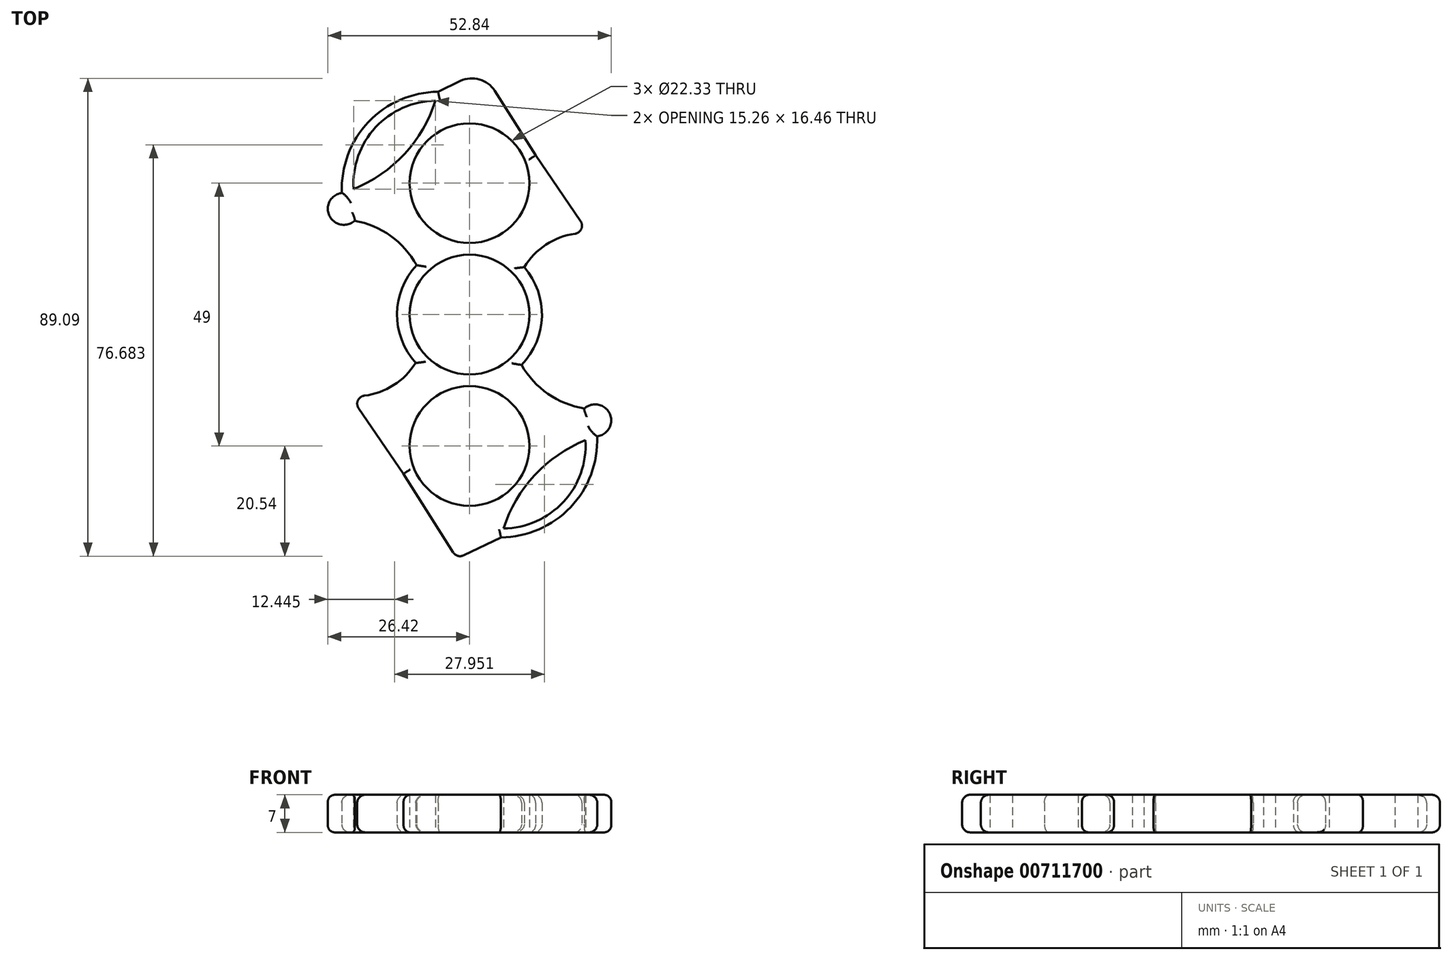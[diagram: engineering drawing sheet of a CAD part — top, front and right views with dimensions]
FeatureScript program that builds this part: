
annotation { "Feature Type Name" : "Feature", "Feature Type Description" : "" }
export const myFeature = defineFeature(function(context is Context, id is Id, definition is map)
    precondition{}
    {
        {
            var Q0;
            Q0=qCreatedBy(makeId("Top.planeOp"),FACE);
            var sketch = newSketch(context, id + "F0", { "sketchPlane" : qUnion([Q0])});
            skCircle(sketch, "E0", {"center": v(0, 0) * mm, "radius": 11.16 * mm});
            skCircle(sketch, "E1", {"center": v(0, 24.5) * mm, "radius": 11.16 * mm});
            skCircle(sketch, "E2", {"center": v(0, 24.5) * mm, "radius": 12.8 * mm});
            skCircle(sketch, "E3", {"center": v(0, 0) * mm, "radius": 13.5 * mm});
            skCircle(sketch, "E4.1.0", {"center": v(0, -24.5) * mm, "radius": 11.16 * mm});
            skCircle(sketch, "E4.1.1", {"center": v(0, -24.5) * mm, "radius": 12.8 * mm});
            skLineSegment(sketch, "E5", {"start": v(12.33, 29.7) * mm, "end": v(22.22, 15.2) * mm});
            skArc(sketch, "E6", {"start": v(-9.87, 9.2) * mm, "mid": v(-14.7, 14.68) * mm, "end": v(-21.43, 17.5) * mm});
            skArc(sketch, "E7", {"start": v(22.22, 15.2) * mm, "mid": v(15.33, 13.68) * mm, "end": v(10.2, 8.84) * mm});
            skArc(sketch, "E8.1.1", {"start": v(9.36, -8.73) * mm, "mid": v(14.33, -14.57) * mm, "end": v(21.43, -17.5) * mm});
            skLineSegment(sketch, "E8.1.2", {"start": v(-12.33, -29.7) * mm, "end": v(-22.22, -15.2) * mm});
            skArc(sketch, "E8.1.3", {"start": v(-22.22, -15.2) * mm, "mid": v(-14.95, -13.62) * mm, "end": v(-9.68, -8.38) * mm});
            skArc(sketch, "E9", {"start": v(-23.8, 22.69) * mm, "mid": v(-23.38, 16.73) * mm, "end": v(-23.15, 22.7) * mm});
            skArc(sketch, "E10", {"start": v(-23.13, 22.85) * mm, "mid": v(-12.1, 29.99) * mm, "end": v(-5.87, 41.55) * mm});
            skLineSegment(sketch, "E11", {"start": v(-5.87, 41.55) * mm, "end": v(2.3, 45.47) * mm});
            skPoint(sketch, "E12.orphan", {"position": v(0, 47.8) * mm});
            skArc(sketch, "E13.1.0", {"start": v(23.8, -22.69) * mm, "mid": v(23.38, -16.73) * mm, "end": v(23.15, -22.7) * mm});
            skArc(sketch, "E13.1.1", {"start": v(23.13, -22.85) * mm, "mid": v(12.1, -29.99) * mm, "end": v(5.87, -41.55) * mm});
            skLineSegment(sketch, "E13.1.2", {"start": v(5.87, -41.55) * mm, "end": v(-2.3, -45.47) * mm});
            skPoint(sketch, "E14.orphan", {"position": v(0, -47.8) * mm});
            skArc(sketch, "E15", {"start": v(-5.87, 41.55) * mm, "mid": v(-18.83, 35.92) * mm, "end": v(-23.8, 22.69) * mm});
            skArc(sketch, "E16.1.1", {"start": v(5.87, -41.55) * mm, "mid": v(18.83, -35.92) * mm, "end": v(23.8, -22.69) * mm});
            skPoint(sketch, "E17.orphan", {"position": v(-23.56, 22.71) * mm});
            skPoint(sketch, "E18.orphan", {"position": v(23.56, -22.71) * mm});
            skPoint(sketch, "E19.orphan", {"position": v(5.87, -41.55) * mm});
            skArc(sketch, "E20.trimOffspring", {"start": v(-23.13, 22.85) * mm, "mid": v(-23.14, 22.78) * mm, "end": v(-23.15, 22.7) * mm});
            skArc(sketch, "E21.trimOffspring", {"start": v(23.13, -22.85) * mm, "mid": v(23.14, -22.78) * mm, "end": v(23.15, -22.7) * mm});
            skArc(sketch, "E22", {"start": v(6.35, -39.87) * mm, "mid": v(17.5, -34.92) * mm, "end": v(21.6, -23.41) * mm});
            skArc(sketch, "E23.1.0", {"start": v(-6.35, 39.87) * mm, "mid": v(-17.5, 34.92) * mm, "end": v(-21.6, 23.41) * mm});
            skLineSegment(sketch, "E24", {"start": v(-23.15, 22.7) * mm, "end": v(-23.8, 22.69) * mm});
            skLineSegment(sketch, "E25", {"start": v(23.8, -22.69) * mm, "end": v(23.15, -22.7) * mm});
            skLineSegment(sketch, "E26", {"start": v(12.33, 29.7) * mm, "end": v(2.3, 45.47) * mm});
            skPoint(sketch, "E27.orphan", {"position": v(6.73, 47.59) * mm});
            skLineSegment(sketch, "E28.1.1", {"start": v(-12.33, -29.7) * mm, "end": v(-2.3, -45.47) * mm});
            skPoint(sketch, "E29.orphan", {"position": v(-6.73, -47.59) * mm});
            skSolve(sketch);
        }
        {
            var Q0;
            {var subQ0=sQuery(id+"F0.wireOp",EDGE,"E9");var subQ1=makeQuery(id+"F0.imprint","INTERSECT",VERTEX,{"derivedFrom":[sQuery(id+"F0.wireOp",EDGE,"E6"),subQ0]});Q0=makeQuery(id+"F0.imprint","IMPRINT",FACE,{"disambiguationData":[TD([[makeQuery(id+"F0.imprint","IMPRINT",EDGE,{"disambiguationData":[TD([[subQ1,1.0]])],"derivedFrom":subQ0}),1.0]])]});}
            var Q1;
            {var subQ0=sQuery(id+"F0.wireOp",EDGE,"E10");var subQ1=sQuery(id+"F0.wireOp",EDGE,"E9");var subQ2=makeQuery(id+"F0.imprint","INTERSECT",VERTEX,{"derivedFrom":[subQ1,subQ0]});Q1=makeQuery(id+"F0.imprint","IMPRINT",FACE,{"disambiguationData":[TD([[makeQuery(id+"F0.imprint","IMPRINT",EDGE,{"disambiguationData":[TD([[subQ2,-1.0]])],"derivedFrom":subQ1}),-1.0]])]});}
            var Q2;
            {var subQ0=sQuery(id+"F0.wireOp",EDGE,"E9");var subQ1=makeQuery(id+"F0.imprint","INTERSECT",VERTEX,{"derivedFrom":[subQ0,sQuery(id+"F0.wireOp",EDGE,"E10")]});Q2=makeQuery(id+"F0.imprint","IMPRINT",FACE,{"disambiguationData":[TD([[makeQuery(id+"F0.imprint","IMPRINT",EDGE,{"disambiguationData":[TD([[subQ1,1.0]])],"derivedFrom":subQ0}),1.0]])]});}
            var Q3;
            {var subQ0=sQuery(id+"F0.wireOp",EDGE,"E10");var subQ1=sQuery(id+"F0.wireOp",EDGE,"E9");var subQ2=makeQuery(id+"F0.imprint","INTERSECT",VERTEX,{"derivedFrom":[subQ1,subQ0]});Q3=makeQuery(id+"F0.imprint","IMPRINT",FACE,{"disambiguationData":[TD([[makeQuery(id+"F0.imprint","IMPRINT",EDGE,{"disambiguationData":[TD([[subQ2,1.0]])],"derivedFrom":subQ1}),-1.0]])]});}
            var Q4;
            {var subQ0=sQuery(id+"F0.wireOp",EDGE,"E13.1.1");var subQ1=sQuery(id+"F0.wireOp",EDGE,"E13.1.0");var subQ2=makeQuery(id+"F0.imprint","INTERSECT",VERTEX,{"derivedFrom":[subQ1,subQ0]});Q4=makeQuery(id+"F0.imprint","IMPRINT",FACE,{"disambiguationData":[TD([[makeQuery(id+"F0.imprint","IMPRINT",EDGE,{"disambiguationData":[TD([[subQ2,1.0]])],"derivedFrom":subQ1}),-1.0]])]});}
            var Q5;
            {var subQ0=sQuery(id+"F0.wireOp",EDGE,"E13.1.0");var subQ1=makeQuery(id+"F0.imprint","INTERSECT",VERTEX,{"derivedFrom":[subQ0,sQuery(id+"F0.wireOp",EDGE,"E13.1.1")]});Q5=makeQuery(id+"F0.imprint","IMPRINT",FACE,{"disambiguationData":[TD([[makeQuery(id+"F0.imprint","IMPRINT",EDGE,{"disambiguationData":[TD([[subQ1,1.0]])],"derivedFrom":subQ0}),1.0]])]});}
            var Q6;
            {var subQ0=sQuery(id+"F0.wireOp",EDGE,"E13.1.1");var subQ1=sQuery(id+"F0.wireOp",EDGE,"E13.1.0");var subQ2=makeQuery(id+"F0.imprint","INTERSECT",VERTEX,{"derivedFrom":[subQ1,subQ0]});Q6=makeQuery(id+"F0.imprint","IMPRINT",FACE,{"disambiguationData":[TD([[makeQuery(id+"F0.imprint","IMPRINT",EDGE,{"disambiguationData":[TD([[subQ2,-1.0]])],"derivedFrom":subQ1}),-1.0]])]});}
            var Q7;
            {var subQ10=sQuery(id+"F0.wireOp",EDGE,"E8.1.1");Q7=makeQuery(id+"F0.imprint","IMPRINT",FACE,{"disambiguationData":[TD([[makeQuery(id+"F0.imprint","IMPRINT",EDGE,{"derivedFrom":subQ10}),-1.0]])]});}
            var Q8;
            Q8=makeQuery(id+"F0.imprint","IMPRINT",FACE,{"disambiguationData":[TD([[makeQuery(id+"F0.imprint","IMPRINT",EDGE,{"derivedFrom":sQuery(id+"F0.wireOp",EDGE,"E4.1.0")}),-1.0]])]});
            var Q9;
            {var subQ0=sQuery(id+"F0.wireOp",EDGE,"E4.1.1");var subQ1=sQuery(id+"F0.wireOp",EDGE,"E3");var subQ2=makeQuery(id+"F0.imprint","INTERSECT",VERTEX,{"disambiguationData":[OD(0.0)],"derivedFrom":[subQ1,subQ0]});Q9=makeQuery(id+"F0.imprint","IMPRINT",FACE,{"disambiguationData":[TD([[makeQuery(id+"F0.imprint","IMPRINT",EDGE,{"disambiguationData":[TD([[subQ2,-1.0]])],"derivedFrom":subQ1}),1.0]])]});}
            var Q10;
            {var subQ0=sQuery(id+"F0.wireOp",EDGE,"E3");var subQ1=sQuery(id+"F0.wireOp",EDGE,"E2");var subQ2=makeQuery(id+"F0.imprint","INTERSECT",VERTEX,{"disambiguationData":[OD(0.0)],"derivedFrom":[subQ1,subQ0]});Q10=makeQuery(id+"F0.imprint","IMPRINT",FACE,{"disambiguationData":[TD([[makeQuery(id+"F0.imprint","IMPRINT",EDGE,{"disambiguationData":[TD([[subQ2,1.0]])],"derivedFrom":subQ1}),1.0]])]});}
            var Q11;
            Q11=makeQuery(id+"F0.imprint","IMPRINT",FACE,{"disambiguationData":[TD([[makeQuery(id+"F0.imprint","IMPRINT",EDGE,{"derivedFrom":sQuery(id+"F0.wireOp",EDGE,"E0")}),-1.0]])]});
            var Q12;
            Q12=makeQuery(id+"F0.imprint","IMPRINT",FACE,{"disambiguationData":[TD([[makeQuery(id+"F0.imprint","IMPRINT",EDGE,{"derivedFrom":sQuery(id+"F0.wireOp",EDGE,"E1")}),-1.0]])]});
            var Q13;
            Q13=makeQuery(id+"F0.imprint","IMPRINT",FACE,{"disambiguationData":[TD([[makeQuery(id+"F0.imprint","IMPRINT",EDGE,{"derivedFrom":sQuery(id+"F0.wireOp",EDGE,"E5")}),-1.0]])]});
            var Q14;
            {var subQ0=sQuery(id+"F0.wireOp",EDGE,"E13.1.0");var subQ1=makeQuery(id+"F0.imprint","INTERSECT",VERTEX,{"derivedFrom":[sQuery(id+"F0.wireOp",EDGE,"E8.1.1"),subQ0]});Q14=makeQuery(id+"F0.imprint","IMPRINT",FACE,{"disambiguationData":[TD([[makeQuery(id+"F0.imprint","IMPRINT",EDGE,{"disambiguationData":[TD([[subQ1,1.0]])],"derivedFrom":subQ0}),1.0]])]});}
            var Q15;
            {var subQ3=sQuery(id+"F0.wireOp",EDGE,"vcktaI46-IUl0-3yXv-VcWj-Kn2E1PGQpO04");Q15=makeQuery(id+"F0.imprint","IMPRINT",FACE,{"disambiguationData":[TD([[makeQuery(id+"F0.imprint","IMPRINT",EDGE,{"derivedFrom":subQ3}),-1.0]])]});}
            var Q16;
            {var subQ5=sQuery(id+"F0.wireOp",EDGE,"ede8bd79-204c-4c09-93b7-07fb39b55257.1.0");Q16=makeQuery(id+"F0.imprint","IMPRINT",FACE,{"disambiguationData":[TD([[makeQuery(id+"F0.imprint","IMPRINT",EDGE,{"derivedFrom":subQ5}),-1.0]])]});}
            var Q17;
            {var subQ3=sQuery(id+"F0.wireOp",EDGE,"41VxDnPx-IEWx-Z7BX-6FUc-ibJ1VB5Gogfi");Q17=makeQuery(id+"F0.imprint","IMPRINT",FACE,{"disambiguationData":[TD([[makeQuery(id+"F0.imprint","IMPRINT",EDGE,{"derivedFrom":subQ3}),-1.0]])]});}
            var Q18;
            {var subQ5=sQuery(id+"F0.wireOp",EDGE,"b636ae70-9769-46bb-8db1-60fec75669ff.1.0");Q18=makeQuery(id+"F0.imprint","IMPRINT",FACE,{"disambiguationData":[TD([[makeQuery(id+"F0.imprint","IMPRINT",EDGE,{"derivedFrom":subQ5}),-1.0]])]});}
            var Q19;
            {var subQ1=sQuery(id+"F0.wireOp",EDGE,"E16.1.1");Q19=makeQuery(id+"F0.imprint","IMPRINT",FACE,{"disambiguationData":[TD([[makeQuery(id+"F0.imprint","IMPRINT",EDGE,{"derivedFrom":subQ1}),1.0]])]});}
            var Q20;
            {var subQ1=sQuery(id+"F0.wireOp",EDGE,"E15");Q20=makeQuery(id+"F0.imprint","IMPRINT",FACE,{"disambiguationData":[TD([[makeQuery(id+"F0.imprint","IMPRINT",EDGE,{"derivedFrom":subQ1}),1.0]])]});}
            extrude(context, id + "F1", {"entities" : qUnion([Q0, Q1, Q2, Q3, Q4, Q5, Q6, Q7, Q8, Q9, Q10, Q11, Q12, Q13, Q14, Q15, Q16, Q17, Q18, Q19, Q20]), "depth" : 7 * mm, "offsetDistance" : 25 * mm});
        }
        {
            var Q0;
            {var subQ0=sQuery(id+"F0.wireOp",EDGE,"E3");Q0=makeQuery(id+"F1.opExtrude","CAP_EDGE",EDGE,{"disambiguationData":[OSD([subQ0]),TDD([makeQuery(id+"F0.imprint","IMPRINT",EDGE,{"disambiguationData":[TD([[makeQuery(id+"F0.imprint","INTERSECT",VERTEX,{"derivedFrom":[subQ0,sQuery(id+"F0.wireOp",EDGE,"E6")]}),-1.0]])],"derivedFrom":subQ0})])],"isStart":false});}
            var Q1;
            {var subQ0=sQuery(id+"F0.wireOp",EDGE,"E3");Q1=makeQuery(id+"F1.opExtrude","CAP_EDGE",EDGE,{"disambiguationData":[OSD([subQ0]),TDD([makeQuery(id+"F0.imprint","IMPRINT",EDGE,{"disambiguationData":[TD([[makeQuery(id+"F0.imprint","INTERSECT",VERTEX,{"derivedFrom":[subQ0,sQuery(id+"F0.wireOp",EDGE,"E6")]}),-1.0]])],"derivedFrom":subQ0})])],"isStart":true});}
            var Q2;
            Q2=makeQuery(id+"F1.opExtrude","CAP_EDGE",EDGE,{"disambiguationData":[OSD([sQuery(id+"F0.wireOp",EDGE,"E8.1.3")])],"isStart":false});
            var Q3;
            Q3=makeQuery(id+"F1.opExtrude","CAP_EDGE",EDGE,{"disambiguationData":[OSD([sQuery(id+"F0.wireOp",EDGE,"E6")])],"isStart":false});
            var Q4;
            Q4=makeQuery(id+"F1.opExtrude","CAP_EDGE",EDGE,{"disambiguationData":[OSD([sQuery(id+"F0.wireOp",EDGE,"E6")])],"isStart":true});
            var Q5;
            Q5=makeQuery(id+"F1.opExtrude","CAP_EDGE",EDGE,{"disambiguationData":[OSD([sQuery(id+"F0.wireOp",EDGE,"E8.1.3")])],"isStart":true});
            var Q6;
            Q6=makeQuery(id+"F1.opExtrude","SWEPT_EDGE",EDGE,{"disambiguationData":[OSD([sQuery(id+"F0.wireOp",EDGE,"E8.1.2"),sQuery(id+"F0.wireOp",EDGE,"E8.1.3")])]});
            var Q7;
            Q7=makeQuery(id+"F1.opExtrude","CAP_EDGE",EDGE,{"disambiguationData":[OSD([sQuery(id+"F0.wireOp",EDGE,"E8.1.2")])],"isStart":false});
            var Q8;
            Q8=makeQuery(id+"F1.opExtrude","CAP_EDGE",EDGE,{"disambiguationData":[OSD([sQuery(id+"F0.wireOp",EDGE,"E8.1.2")])],"isStart":true});
            var Q9;
            Q9=makeQuery(id+"F1.opExtrude","CAP_EDGE",EDGE,{"disambiguationData":[OSD([sQuery(id+"F0.wireOp",EDGE,"E13.1.3")])],"isStart":false});
            var Q10;
            Q10=makeQuery(id+"F1.opExtrude","SWEPT_EDGE",EDGE,{"disambiguationData":[OSD([sQuery(id+"F0.wireOp",EDGE,"E13.1.2"),sQuery(id+"F0.wireOp",EDGE,"E13.1.3")])]});
            var Q11;
            Q11=makeQuery(id+"F1.opExtrude","CAP_EDGE",EDGE,{"disambiguationData":[OSD([sQuery(id+"F0.wireOp",EDGE,"E13.1.2")])],"isStart":false});
            var Q12;
            Q12=makeQuery(id+"F1.opExtrude","CAP_EDGE",EDGE,{"disambiguationData":[OSD([sQuery(id+"F0.wireOp",EDGE,"E13.1.2")])],"isStart":true});
            var Q13;
            Q13=makeQuery(id+"F1.opExtrude","CAP_EDGE",EDGE,{"disambiguationData":[OSD([sQuery(id+"F0.wireOp",EDGE,"E16.1.1")])],"isStart":false});
            var Q14;
            Q14=makeQuery(id+"F1.opExtrude","CAP_EDGE",EDGE,{"disambiguationData":[OSD([sQuery(id+"F0.wireOp",EDGE,"E16.1.1")])],"isStart":true});
            var Q15;
            Q15=makeQuery(id+"F1.opExtrude","CAP_EDGE",EDGE,{"disambiguationData":[OSD([sQuery(id+"F0.wireOp",EDGE,"E8.1.1")])],"isStart":false});
            var Q16;
            {var subQ0=sQuery(id+"F0.wireOp",EDGE,"E3");Q16=makeQuery(id+"F1.opExtrude","CAP_EDGE",EDGE,{"disambiguationData":[OSD([subQ0]),TDD([makeQuery(id+"F0.imprint","IMPRINT",EDGE,{"disambiguationData":[TD([[makeQuery(id+"F0.imprint","INTERSECT",VERTEX,{"derivedFrom":[subQ0,sQuery(id+"F0.wireOp",EDGE,"E7")]}),1.0]])],"derivedFrom":subQ0})])],"isStart":false});}
            var Q17;
            Q17=makeQuery(id+"F1.opExtrude","CAP_EDGE",EDGE,{"disambiguationData":[OSD([sQuery(id+"F0.wireOp",EDGE,"E8.1.1")])],"isStart":true});
            var Q18;
            {var subQ0=sQuery(id+"F0.wireOp",EDGE,"E3");Q18=makeQuery(id+"F1.opExtrude","CAP_EDGE",EDGE,{"disambiguationData":[OSD([subQ0]),TDD([makeQuery(id+"F0.imprint","IMPRINT",EDGE,{"disambiguationData":[TD([[makeQuery(id+"F0.imprint","INTERSECT",VERTEX,{"derivedFrom":[subQ0,sQuery(id+"F0.wireOp",EDGE,"E7")]}),1.0]])],"derivedFrom":subQ0})])],"isStart":true});}
            var Q19;
            Q19=makeQuery(id+"F1.opExtrude","CAP_EDGE",EDGE,{"disambiguationData":[OSD([sQuery(id+"F0.wireOp",EDGE,"E7")])],"isStart":true});
            var Q20;
            Q20=makeQuery(id+"F1.opExtrude","SWEPT_EDGE",EDGE,{"disambiguationData":[OSD([sQuery(id+"F0.wireOp",EDGE,"E5"),sQuery(id+"F0.wireOp",EDGE,"E7")])]});
            var Q21;
            Q21=makeQuery(id+"F1.opExtrude","CAP_EDGE",EDGE,{"disambiguationData":[OSD([sQuery(id+"F0.wireOp",EDGE,"E5")])],"isStart":true});
            var Q22;
            Q22=makeQuery(id+"F1.opExtrude","CAP_EDGE",EDGE,{"disambiguationData":[OSD([sQuery(id+"F0.wireOp",EDGE,"Zcna8AMt-cuaw-Y1I0-uXds-u55liH3GFgRk")])],"isStart":true});
            var Q23;
            Q23=makeQuery(id+"F1.opExtrude","CAP_EDGE",EDGE,{"disambiguationData":[OSD([sQuery(id+"F0.wireOp",EDGE,"E11")])],"isStart":true});
            var Q24;
            Q24=makeQuery(id+"F1.opExtrude","CAP_EDGE",EDGE,{"disambiguationData":[OSD([sQuery(id+"F0.wireOp",EDGE,"Zcna8AMt-cuaw-Y1I0-uXds-u55liH3GFgRk")])],"isStart":false});
            var Q25;
            Q25=makeQuery(id+"F1.opExtrude","CAP_EDGE",EDGE,{"disambiguationData":[OSD([sQuery(id+"F0.wireOp",EDGE,"E5")])],"isStart":false});
            var Q26;
            Q26=makeQuery(id+"F1.opExtrude","CAP_EDGE",EDGE,{"disambiguationData":[OSD([sQuery(id+"F0.wireOp",EDGE,"E7")])],"isStart":false});
            var Q27;
            Q27=makeQuery(id+"F1.opExtrude","CAP_EDGE",EDGE,{"disambiguationData":[OSD([sQuery(id+"F0.wireOp",EDGE,"E11")])],"isStart":false});
            var Q28;
            Q28=makeQuery(id+"F1.opExtrude","CAP_EDGE",EDGE,{"disambiguationData":[OSD([sQuery(id+"F0.wireOp",EDGE,"E15")])],"isStart":true});
            var Q29;
            Q29=makeQuery(id+"F1.opExtrude","CAP_EDGE",EDGE,{"disambiguationData":[OSD([sQuery(id+"F0.wireOp",EDGE,"E15")])],"isStart":false});
            var Q30;
            Q30=makeQuery(id+"F1.opExtrude","CAP_EDGE",EDGE,{"disambiguationData":[OSD([sQuery(id+"F0.wireOp",EDGE,"E13.1.3")])],"isStart":true});
            var Q31;
            Q31=makeQuery(id+"F1.opExtrude","CAP_EDGE",EDGE,{"disambiguationData":[OSD([sQuery(id+"F0.wireOp",EDGE,"E13.1.2")])],"isStart":false});
            var Q32;
            Q32=makeQuery(id+"F1.opExtrude","CAP_EDGE",EDGE,{"disambiguationData":[OSD([sQuery(id+"F0.wireOp",EDGE,"E13.1.2")])],"isStart":true});
            fillet(context, id + "F2", {"entities" : qUnion([Q0, Q1, Q2, Q3, Q4, Q5, Q6, Q7, Q8, Q9, Q10, Q11, Q12, Q13, Q14, Q15, Q16, Q17, Q18, Q19, Q20, Q21, Q22, Q23, Q24, Q25, Q26, Q27, Q28, Q29, Q30, Q31, Q32]), "radius" : 1.5 * mm, "tangentPropagation" : true, "allowEdgeOverflow" : false});
        }
        {
            var Q0;
            Q0=makeQuery(id+"F1.opExtrude","CAP_EDGE",EDGE,{"disambiguationData":[OSD([sQuery(id+"F0.wireOp",EDGE,"E9")])],"isStart":false});
            var Q1;
            Q1=makeQuery(id+"F1.opExtrude","CAP_EDGE",EDGE,{"disambiguationData":[OSD([sQuery(id+"F0.wireOp",EDGE,"E9")])],"isStart":true});
            var Q2;
            Q2=makeQuery(id+"F1.opExtrude","CAP_EDGE",EDGE,{"disambiguationData":[OSD([sQuery(id+"F0.wireOp",EDGE,"E13.1.0")])],"isStart":false});
            var Q3;
            Q3=makeQuery(id+"F1.opExtrude","CAP_EDGE",EDGE,{"disambiguationData":[OSD([sQuery(id+"F0.wireOp",EDGE,"E13.1.0")])],"isStart":true});
            fillet(context, id + "F3", {"entities" : qUnion([Q0, Q1, Q2, Q3]), "radius" : 1.3 * mm, "tangentPropagation" : true, "allowEdgeOverflow" : false});
        }
        {
            var Q0;
            Q0=makeQuery(id+"F1.opExtrude","SWEPT_EDGE",EDGE,{"disambiguationData":[OSD([sQuery(id+"F0.wireOp",EDGE,"E13.1.2"),sQuery(id+"F0.wireOp",EDGE,"E28.1.1")])]});
            var Q1;
            {var subQ0=sQuery(id+"F0.wireOp",EDGE,"E26");var subQ1=sQuery(id+"F0.wireOp",EDGE,"E11");Q1=makeQuery(id+"F2.opFillet","BLEND_FACE",FACE,{"disambiguationData":[OSD([subQ1,subQ0]),TDD([makeQuery(id+"F1.opExtrude","SWEPT_EDGE",EDGE,{"disambiguationData":[OSD([subQ1,subQ0])]})])]});}
            var Q2;
            Q2=makeQuery(id+"F1.opExtrude","SWEPT_EDGE",EDGE,{"disambiguationData":[OSD([sQuery(id+"F0.wireOp",EDGE,"E11"),sQuery(id+"F0.wireOp",EDGE,"E26")])]});
            fillet(context, id + "F4", {"entities" : qUnion([Q0, Q1, Q2]), "radius" : 5 * mm, "tangentPropagation" : true, "allowEdgeOverflow" : false});
        }
    });
